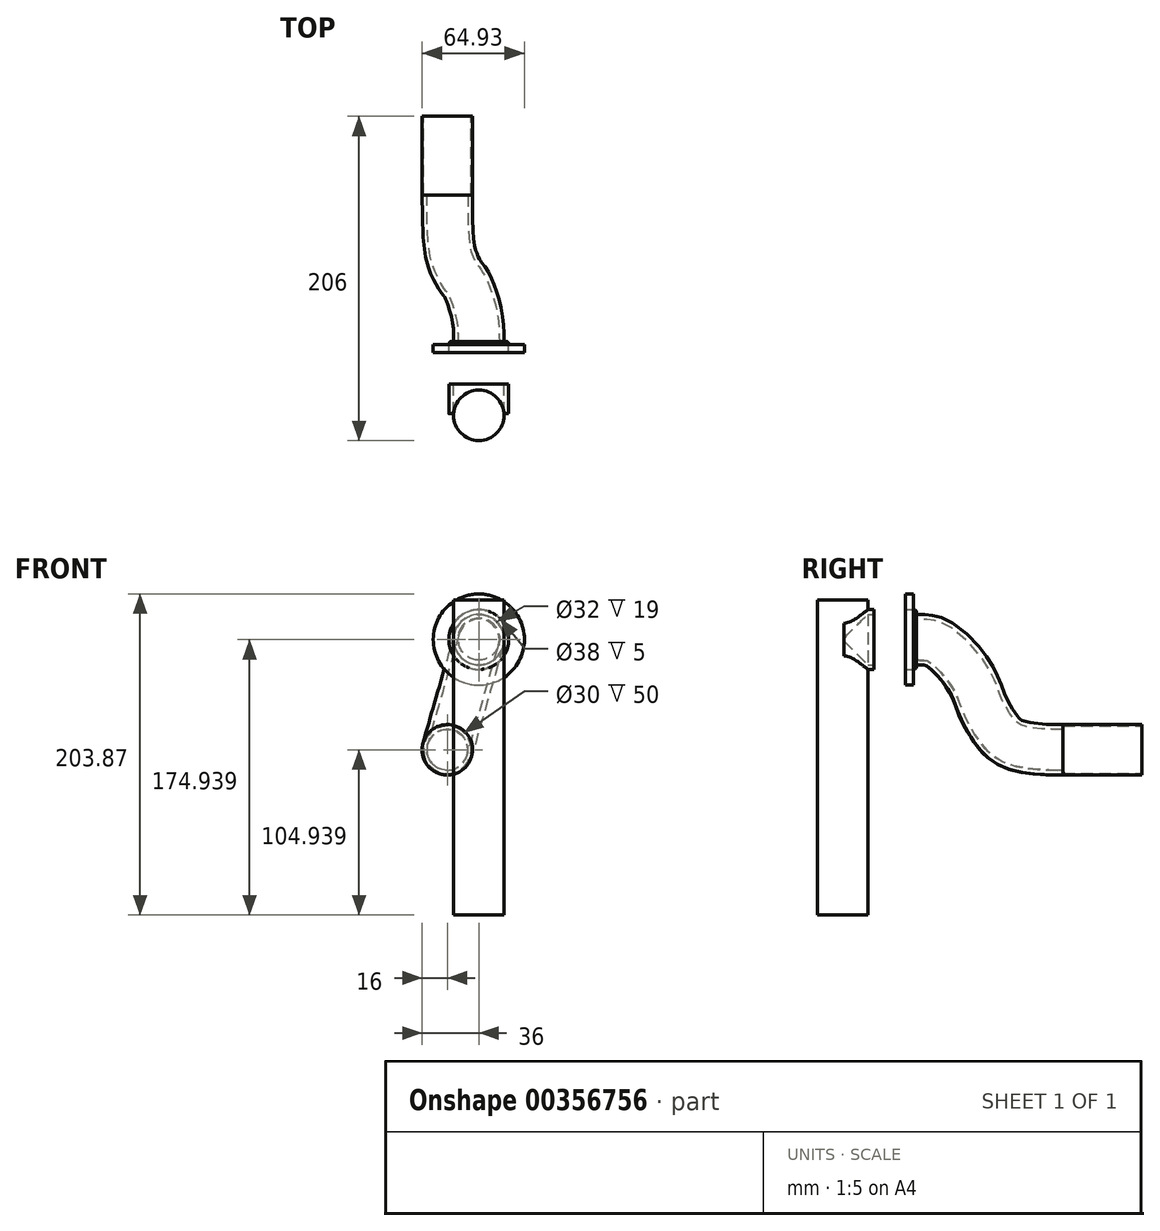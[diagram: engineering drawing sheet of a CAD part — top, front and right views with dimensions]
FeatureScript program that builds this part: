
annotation { "Feature Type Name" : "Feature", "Feature Type Description" : "" }
export const myFeature = defineFeature(function(context is Context, id is Id, definition is map)
    precondition{}
    {
        {
            var Q0;
            Q0=qCreatedBy(makeId("Front.planeOp"),FACE);
            var sketch = newSketch(context, id + "F0", { "sketchPlane" : qUnion([Q0])});
            skCircle(sketch, "E0", {"center": v(-20, 4.94) * mm, "radius": 16 * mm});
            skCircle(sketch, "E1", {"center": v(-20, 4.94) * mm, "radius": 20 * mm});
            skCircle(sketch, "E2", {"center": v(-20, 4.94) * mm, "radius": 15 * mm});
            skSolve(sketch);
        }
        {
            var Q0;
            Q0=makeQuery(id+"F0.imprint","IMPRINT",FACE,{"disambiguationData":[TD([[makeQuery(id+"F0.imprint","IMPRINT",EDGE,{"derivedFrom":sQuery(id+"F0.wireOp",EDGE,"E0")}),1.0]])]});
            extrude(context, id + "F1", {"entities" : qUnion([Q0]), "depth" : 50 * mm});
        }
        {
            var Q0;
            Q0=qCreatedBy(makeId("Top.planeOp"),FACE);
            var sketch = newSketch(context, id + "F2", { "sketchPlane" : qUnion([Q0])});
            skLineSegment(sketch, "E3", {"start": v(146.77, -190) * mm, "end": v(-145.9, -190) * mm, "construction": true});
            skCircle(sketch, "E4", {"center": v(0, -190) * mm, "radius": 16 * mm});
            skSolve(sketch);
        }
        {
            var Q0;
            Q0=makeQuery(id+"F2.imprint","IMPRINT",FACE,{"disambiguationData":[TD([[makeQuery(id+"F2.imprint","IMPRINT",EDGE,{"derivedFrom":sQuery(id+"F2.wireOp",EDGE,"E4")}),1.0]])]});
            extrude(context, id + "F3", {"entities" : qUnion([Q0]), "endBound" : BoundingType.SYMMETRIC, "depth" : 200 * mm});
        }
        {
            var Q0;
            Q0=qCreatedBy(makeId("Front.planeOp"),FACE);
            cPlane(context, id + "F4", {"entities" : qUnion([Q0]), "cplaneType" : CPlaneType.OFFSET, "offset" : 174 * mm, "width" : 150 * mm, "height" : 150 * mm});
        }
        {
            var Q0;
            Q0=qCreatedBy(id+"F4.planeOp",FACE);
            var sketch = newSketch(context, id + "F5", { "sketchPlane" : qUnion([Q0])});
            skLineSegment(sketch, "E5", {"start": v(73.93, 74.94) * mm, "end": v(-93, 74.94) * mm, "construction": true});
            skCircle(sketch, "E6", {"center": v(0, 74.94) * mm, "radius": 19 * mm});
            skCircle(sketch, "E7", {"center": v(0, 74.94) * mm, "radius": 16 * mm});
            skCircle(sketch, "E8", {"center": v(0, 74.94) * mm, "radius": 29 * mm});
            skSolve(sketch);
        }
        {
            var Q0;
            Q0=makeQuery(id+"F5.imprint","IMPRINT",FACE,{"disambiguationData":[TD([[makeQuery(id+"F5.imprint","IMPRINT",EDGE,{"derivedFrom":sQuery(id+"F5.wireOp",EDGE,"E6")}),1.0]])]});
            extrude(context, id + "F6", {"entities" : qUnion([Q0]), "operationType" : NewBodyOperationType.ADD, "depth" : 15 * mm, "hasSecondDirection" : true, "secondDirectionOppositeDirection" : true, "secondDirectionDepth" : 29 * mm});
        }
        {
            var Q0;
            Q0=makeQuery(id+"F6.opExtrude","CAP_FACE",FACE,{"disambiguationData":[OSD([sQuery(id+"F5.wireOp",EDGE,"E6"),sQuery(id+"F5.wireOp",EDGE,"E7")])],"isStart":true});
            var sketch = newSketch(context, id + "F7", { "sketchPlane" : qUnion([Q0])});
            skCircle(sketch, "E9", {"center": v(0, 74.94) * mm, "radius": 28.93 * mm});
            skCircle(sketch, "E10.0", {"center": v(0, 74.94) * mm, "radius": 19 * mm});
            skCircle(sketch, "E11", {"center": v(0, 74.94) * mm, "radius": 13.5 * mm});
            skSolve(sketch);
        }
        {
            var Q0;
            Q0=makeQuery(id+"F7.imprint","IMPRINT",FACE,{"disambiguationData":[TD([[makeQuery(id+"F7.imprint","IMPRINT",EDGE,{"derivedFrom":sQuery(id+"F7.wireOp",EDGE,"E9")}),1.0]])]});
            extrude(context, id + "F8", {"entities" : qUnion([Q0]), "operationType" : NewBodyOperationType.ADD, "oppositeDirection" : true, "depth" : 5 * mm});
        }
        {
            var Q0;
            Q0=makeQuery(id+"F1.opExtrude","CAP_FACE",FACE,{"disambiguationData":[OSD([sQuery(id+"F0.wireOp",EDGE,"E0"),sQuery(id+"F0.wireOp",EDGE,"E2")])],"isStart":false});
            var sketch = newSketch(context, id + "F9", { "sketchPlane" : qUnion([Q0])});
            skCircle(sketch, "E12.0", {"center": v(-20, 4.94) * mm, "radius": 15 * mm});
            skCircle(sketch, "E13.0", {"center": v(-20, 4.94) * mm, "radius": 16 * mm});
            skCircle(sketch, "E14", {"center": v(-20, 4.94) * mm, "radius": 13 * mm});
            skSolve(sketch);
        }
        {
            var Q0;
            Q0=sQuery(id+"F9.wireOp",VERTEX,"E12.0.center");
            var Q1;
            Q1=sQuery(id+"F7.wireOp",VERTEX,"E10.0.center");
            var Q2;
            Q2=sQuery(id+"F0.wireOp",VERTEX,"E0.center");
            cPlane(context, id + "F10", {"entities" : qUnion([Q0, Q1, Q2]), "cplaneType" : CPlaneType.THREE_POINT, "offset" : 25 * mm, "width" : 150 * mm, "height" : 150 * mm});
        }
        {
            var Q0;
            Q0=qCreatedBy(id+"F10.planeOp",FACE);
            var sketch = newSketch(context, id + "F11", { "sketchPlane" : qUnion([Q0])});
            skLineSegment(sketch, "E15", {"start": v(54.39, 72.06) * mm, "end": v(-222.11, 72.06) * mm, "construction": true});
            skLineSegment(sketch, "E16", {"start": v(-145, 179.02) * mm, "end": v(-145, -46.89) * mm, "construction": true});
            skLineSegment(sketch, "E17", {"start": v(-50, 177.68) * mm, "end": v(-50, -70.85) * mm, "construction": true});
            skLineSegment(sketch, "E18", {"start": v(24.43, -0.75) * mm, "end": v(-110.05, -0.75) * mm, "construction": true});
            skFitSpline(sketch, "E19", {"points": [v(-50, -0.75) * mm, v(-79.28, 2.14) * mm, v(-92.3, 12.3) * mm, v(-101.73, 29.67) * mm, v(-108.18, 45.6) * mm, v(-130.44, 70) * mm, v(-145, 72.06) * mm], "startDerivative": vector(-112.58, -1.1) * mm, "endDerivative": vector(-98.84, 8.97) * mm});
            skSolve(sketch);
        }
        {
            var Q0;
            Q0=sQuery(id+"F11.wireOp",EDGE,"E19");
            var Q1;
            Q1=sQuery(id+"F11.wireOp",VERTEX,"E19.start");
            cPlane(context, id + "F12", {"entities" : qUnion([Q0, Q1]), "cplaneType" : CPlaneType.CURVE_POINT, "offset" : 25 * mm, "width" : 150 * mm, "height" : 150 * mm});
        }
        {
            var Q0;
            Q0=qCreatedBy(id+"F12.planeOp",FACE);
            var sketch = newSketch(context, id + "F13", { "sketchPlane" : qUnion([Q0])});
            skCircle(sketch, "E20", {"center": v(-19.87, 5.4) * mm, "radius": 13 * mm});
            skCircle(sketch, "E21", {"center": v(-19.87, 5.4) * mm, "radius": 16 * mm});
            skSolve(sketch);
        }
        {
            var Q0;
            Q0=makeQuery(id+"F13.imprint","IMPRINT",FACE,{"disambiguationData":[TD([[makeQuery(id+"F13.imprint","IMPRINT",EDGE,{"derivedFrom":sQuery(id+"F13.wireOp",EDGE,"E20")}),-1.0]])]});
            var Q1;
            Q1=sQuery(id+"F11.wireOp",EDGE,"E19");
            sweep(context, id + "F14", {"profiles" : qUnion([Q0]), "path" : qUnion([Q1])});
        }
        {
            var Q0;
            Q0=makeQuery(id+"F7.imprint","IMPRINT",FACE,{"disambiguationData":[TD([[makeQuery(id+"F7.imprint","IMPRINT",EDGE,{"derivedFrom":sQuery(id+"F7.wireOp",EDGE,"E10.0")}),-1.0]])]});
            var Q1;
            Q1=makeQuery(id+"F7.imprint","IMPRINT",FACE,{"disambiguationData":[TD([[makeQuery(id+"F7.imprint","IMPRINT",EDGE,{"derivedFrom":sQuery(id+"F7.wireOp",EDGE,"E11")}),-1.0]])]});
            extrude(context, id + "F15", {"entities" : qUnion([Q0, Q1]), "operationType" : NewBodyOperationType.ADD, "depth" : 2 * mm});
        }
        {
            var Q0;
            Q0=makeQuery(id+"F7.imprint","IMPRINT",FACE,{"disambiguationData":[TD([[makeQuery(id+"F7.imprint","IMPRINT",EDGE,{"derivedFrom":sQuery(id+"F7.wireOp",EDGE,"E11")}),-1.0]])]});
            var Q1;
            Q1=makeQuery(id+"F7.imprint","IMPRINT",FACE,{"disambiguationData":[TD([[makeQuery(id+"F7.imprint","IMPRINT",EDGE,{"derivedFrom":sQuery(id+"F7.wireOp",EDGE,"E10.0")}),-1.0]])]});
            var Q2;
            Q2=makeQuery(id+"F7.imprint","IMPRINT",FACE,{"disambiguationData":[TD([[makeQuery(id+"F7.imprint","IMPRINT",EDGE,{"derivedFrom":sQuery(id+"F7.wireOp",EDGE,"E11")}),1.0]])]});
            extrude(context, id + "F16", {"entities" : qUnion([Q0, Q1, Q2]), "operationType" : NewBodyOperationType.REMOVE, "oppositeDirection" : true, "depth" : 25 * mm});
        }
        {
            var Q0;
            Q0=makeQuery(id+"F15.opExtrude","CAP_EDGE",EDGE,{"disambiguationData":[OSD([sQuery(id+"F7.wireOp",EDGE,"E10.0")])],"isStart":false});
            fillet(context, id + "F17", {"entities" : qUnion([Q0]), "radius" : 2 * mm, "rho" : 0.5, "crossSection" : FilletCrossSection.CONIC, "allowEdgeOverflow" : false});
        }
    });
